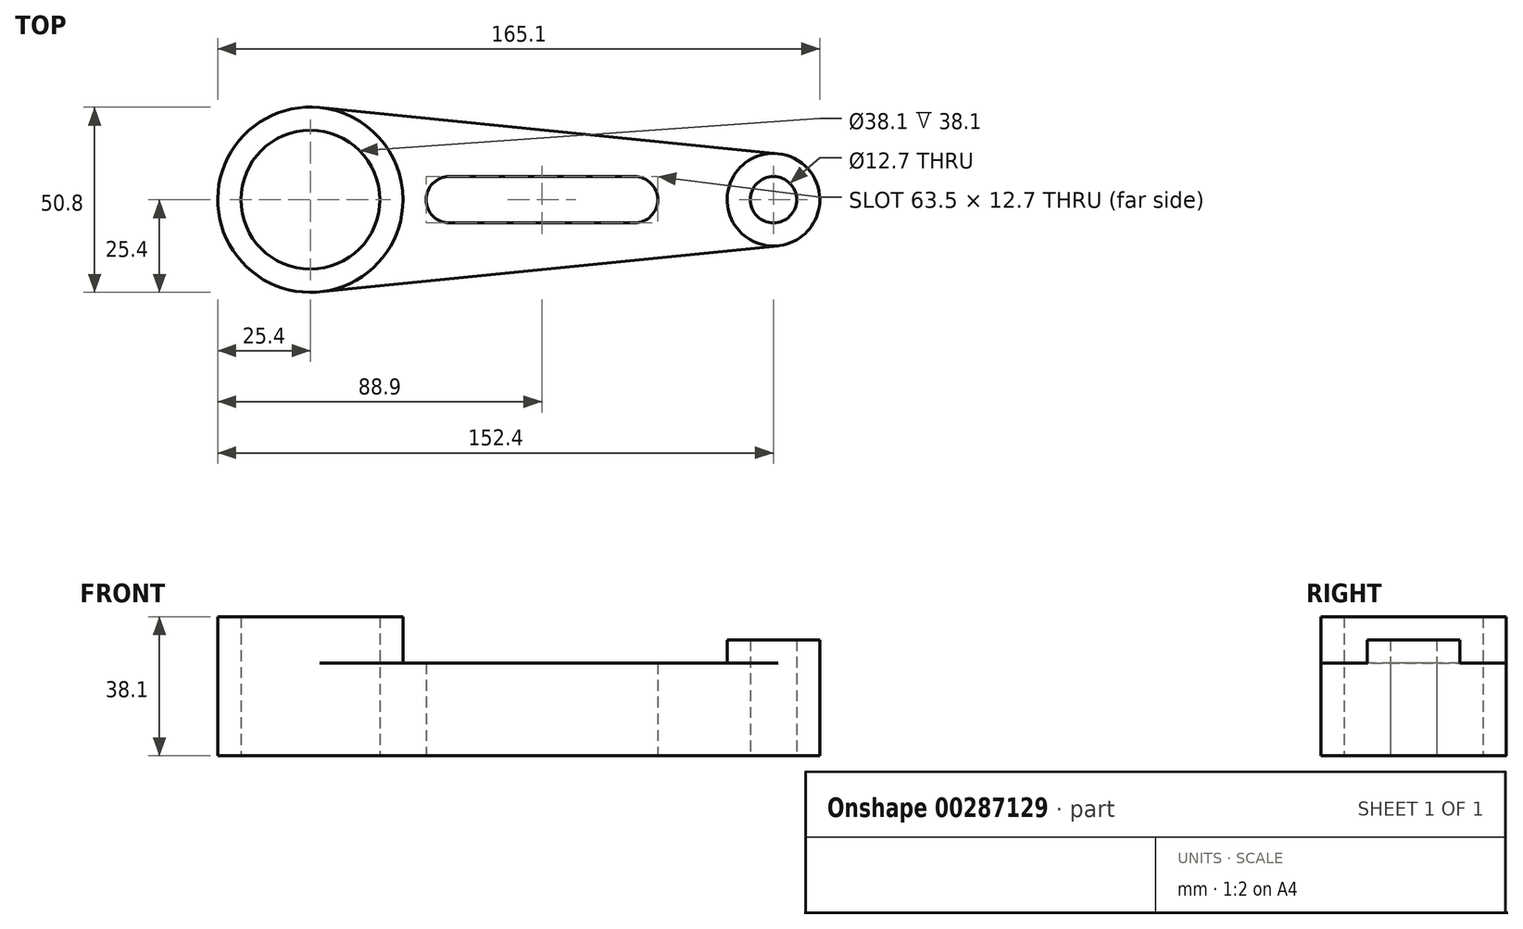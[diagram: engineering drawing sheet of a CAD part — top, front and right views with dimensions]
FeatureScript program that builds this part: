
annotation { "Feature Type Name" : "Feature", "Feature Type Description" : "" }
export const myFeature = defineFeature(function(context is Context, id is Id, definition is map)
    precondition{}
    {
        {
            var Q0;
            Q0=qCreatedBy(makeId("Top.planeOp"),FACE);
            var sketch = newSketch(context, id + "F0", { "sketchPlane" : qUnion([Q0])});
            skCircle(sketch, "E0", {"center": v(-38.1, 0) * mm, "radius": 19.05 * mm});
            skCircle(sketch, "E1", {"center": v(-38.1, 0) * mm, "radius": 25.4 * mm});
            skCircle(sketch, "E2", {"center": v(88.9, 0) * mm, "radius": 12.7 * mm});
            skArc(sketch, "E3", {"start": v(0, 6.35) * mm, "mid": v(-6.35, 0) * mm, "end": v(0, -6.35) * mm});
            skArc(sketch, "E4", {"start": v(50.8, -6.35) * mm, "mid": v(57.15, 0) * mm, "end": v(50.8, 6.35) * mm});
            skLineSegment(sketch, "E5", {"start": v(0, 6.35) * mm, "end": v(50.8, 6.35) * mm});
            skLineSegment(sketch, "E6", {"start": v(0, -6.35) * mm, "end": v(50.8, -6.35) * mm});
            skLineSegment(sketch, "E7", {"start": v(-35.56, 25.27) * mm, "end": v(90.17, 12.64) * mm});
            skLineSegment(sketch, "E8", {"start": v(-35.56, -25.27) * mm, "end": v(90.17, -12.64) * mm});
            skCircle(sketch, "E9", {"center": v(88.9, 0) * mm, "radius": 6.35 * mm});
            skSolve(sketch);
        }
        {
            var Q0;
            Q0=makeQuery(id+"F0.imprint","IMPRINT",FACE,{"disambiguationData":[TD([[makeQuery(id+"F0.imprint","IMPRINT",EDGE,{"derivedFrom":sQuery(id+"F0.wireOp",EDGE,"E0")}),-1.0]])]});
            extrude(context, id + "F1", {"entities" : qUnion([Q0]), "depth" : 38.1 * mm});
        }
        {
            var Q0;
            Q0=makeQuery(id+"F0.imprint","IMPRINT",FACE,{"disambiguationData":[TD([[makeQuery(id+"F0.imprint","IMPRINT",EDGE,{"derivedFrom":sQuery(id+"F0.wireOp",EDGE,"E3")}),-1.0]])]});
            extrude(context, id + "F2", {"entities" : qUnion([Q0]), "operationType" : NewBodyOperationType.ADD, "depth" : 25.4 * mm});
        }
        {
            var Q0;
            Q0=makeQuery(id+"F0.imprint","IMPRINT",FACE,{"disambiguationData":[TD([[makeQuery(id+"F0.imprint","IMPRINT",EDGE,{"derivedFrom":sQuery(id+"F0.wireOp",EDGE,"E9")}),-1.0]])]});
            extrude(context, id + "F3", {"entities" : qUnion([Q0]), "operationType" : NewBodyOperationType.ADD, "depth" : 31.75 * mm});
        }
    });
